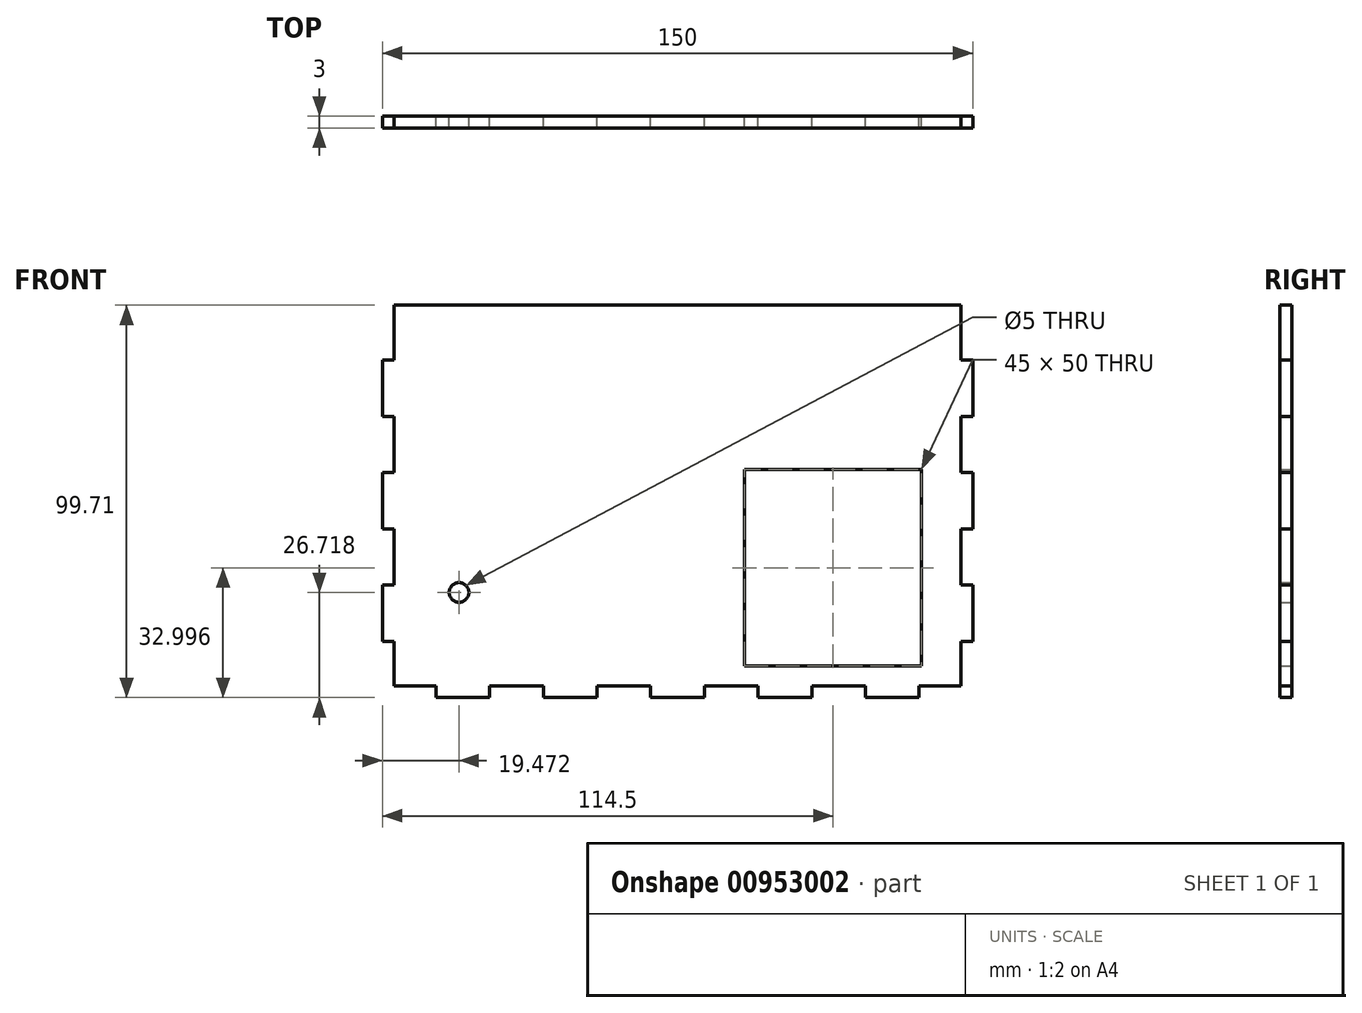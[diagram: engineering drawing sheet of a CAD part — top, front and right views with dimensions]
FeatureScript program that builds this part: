
annotation { "Feature Type Name" : "Feature", "Feature Type Description" : "" }
export const myFeature = defineFeature(function(context is Context, id is Id, definition is map)
    precondition{}
    {
        {
            var Q0;
            Q0=qCreatedBy(makeId("Front.planeOp"),FACE);
            var sketch = newSketch(context, id + "F0", { "sketchPlane" : qUnion([Q0])});
            skLineSegment(sketch, "E0.top", {"start": v(72, 50) * mm, "end": v(-72, 50) * mm});
            skLineSegment(sketch, "E1.bottom", {"start": v(61.36, -49.71) * mm, "end": v(47.73, -49.71) * mm});
            skLineSegment(sketch, "E2", {"start": v(-72, -46.71) * mm, "end": v(-61.36, -46.71) * mm});
            skLineSegment(sketch, "E3", {"start": v(-61.36, -46.71) * mm, "end": v(-61.36, -49.71) * mm});
            skLineSegment(sketch, "E4", {"start": v(-47.73, -46.71) * mm, "end": v(-47.73, -49.71) * mm});
            skLineSegment(sketch, "E5", {"start": v(-34.1, -46.71) * mm, "end": v(-34.1, -49.71) * mm});
            skLineSegment(sketch, "E6", {"start": v(-20.45, -46.71) * mm, "end": v(-20.45, -49.71) * mm});
            skLineSegment(sketch, "E7", {"start": v(-6.82, -46.71) * mm, "end": v(-6.82, -49.71) * mm});
            skLineSegment(sketch, "E8", {"start": v(6.82, -46.71) * mm, "end": v(6.82, -49.71) * mm});
            skLineSegment(sketch, "E9", {"start": v(34.1, -46.71) * mm, "end": v(34.1, -49.71) * mm});
            skLineSegment(sketch, "E10", {"start": v(47.73, -46.71) * mm, "end": v(47.73, -49.71) * mm});
            skLineSegment(sketch, "E11", {"start": v(20.45, -46.71) * mm, "end": v(20.45, -49.71) * mm});
            skLineSegment(sketch, "E12", {"start": v(61.36, -46.71) * mm, "end": v(61.36, -49.71) * mm});
            skLineSegment(sketch, "E13.trimOffspring", {"start": v(-47.73, -46.71) * mm, "end": v(-34.1, -46.71) * mm});
            skLineSegment(sketch, "E14.trimOffspring", {"start": v(-47.73, -49.71) * mm, "end": v(-61.36, -49.71) * mm});
            skLineSegment(sketch, "E15.trimOffspring", {"start": v(-20.45, -46.71) * mm, "end": v(-6.82, -46.71) * mm});
            skLineSegment(sketch, "E16.trimOffspring", {"start": v(-20.45, -49.71) * mm, "end": v(-34.1, -49.71) * mm});
            skLineSegment(sketch, "E17.trimOffspring", {"start": v(6.82, -46.71) * mm, "end": v(20.45, -46.71) * mm});
            skLineSegment(sketch, "E18.trimOffspring", {"start": v(6.82, -49.71) * mm, "end": v(-6.82, -49.71) * mm});
            skLineSegment(sketch, "E19.trimOffspring", {"start": v(34.1, -46.71) * mm, "end": v(47.73, -46.71) * mm});
            skLineSegment(sketch, "E20.trimOffspring", {"start": v(34.1, -49.71) * mm, "end": v(20.45, -49.71) * mm});
            skLineSegment(sketch, "E21.trimOffspring", {"start": v(61.36, -46.71) * mm, "end": v(72, -46.71) * mm});
            skPoint(sketch, "E22.orphan", {"position": v(-72.02, -53.11) * mm});
            skPoint(sketch, "E0.right.start.orphan", {"position": v(-75, -50) * mm});
            skLineSegment(sketch, "E23.right", {"start": v(-75, -35.43) * mm, "end": v(-75, -21.14) * mm});
            skPoint(sketch, "E24.orphan", {"position": v(-75, -49.71) * mm});
            skLineSegment(sketch, "E25", {"start": v(-72, 50.29) * mm, "end": v(-72, 36) * mm});
            skLineSegment(sketch, "E26", {"start": v(-75, 36) * mm, "end": v(-72, 36) * mm});
            skLineSegment(sketch, "E27", {"start": v(-75, 21.71) * mm, "end": v(-72, 21.71) * mm});
            skLineSegment(sketch, "E28", {"start": v(-75, 7.43) * mm, "end": v(-72, 7.43) * mm});
            skLineSegment(sketch, "E29", {"start": v(-75, -6.86) * mm, "end": v(-72, -6.86) * mm});
            skLineSegment(sketch, "E30", {"start": v(-75, -21.14) * mm, "end": v(-72, -21.14) * mm});
            skLineSegment(sketch, "E31", {"start": v(-75, -35.43) * mm, "end": v(-72, -35.43) * mm});
            skLineSegment(sketch, "E32.trimOffspring", {"start": v(-72, -35.43) * mm, "end": v(-72, -46.71) * mm});
            skLineSegment(sketch, "E33.trimOffspring", {"start": v(-75, -6.86) * mm, "end": v(-75, 7.43) * mm});
            skLineSegment(sketch, "E34.trimOffspring", {"start": v(-72, -6.86) * mm, "end": v(-72, -21.14) * mm});
            skLineSegment(sketch, "E35.trimOffspring", {"start": v(-75, 21.71) * mm, "end": v(-75, 36) * mm});
            skLineSegment(sketch, "E36.trimOffspring", {"start": v(-72, 21.71) * mm, "end": v(-72, 7.43) * mm});
            skPoint(sketch, "E37.orphan", {"position": v(-75, 50.29) * mm});
            skPoint(sketch, "E38.orphan", {"position": v(-75, 50) * mm});
            skPoint(sketch, "E39.orphan", {"position": v(75, -50) * mm});
            skLineSegment(sketch, "E40.MirrorCS", {"start": v(75, 36) * mm, "end": v(72, 36) * mm});
            skLineSegment(sketch, "E41.MirrorCS", {"start": v(75, -21.14) * mm, "end": v(72, -21.14) * mm});
            skLineSegment(sketch, "E42.MirrorCS", {"start": v(75, 21.71) * mm, "end": v(72, 21.71) * mm});
            skLineSegment(sketch, "E43.MirrorCS", {"start": v(75, -35.43) * mm, "end": v(72, -35.43) * mm});
            skLineSegment(sketch, "E44.MirrorCS", {"start": v(75, 7.43) * mm, "end": v(72, 7.43) * mm});
            skLineSegment(sketch, "E45.MirrorCS", {"start": v(75, -6.86) * mm, "end": v(72, -6.86) * mm});
            skPoint(sketch, "E46.MirrorP", {"position": v(75, 50) * mm});
            skLineSegment(sketch, "E47.MirrorCS", {"start": v(72, -6.86) * mm, "end": v(72, -21.14) * mm});
            skLineSegment(sketch, "E48.MirrorCS", {"start": v(72, 50.29) * mm, "end": v(72, 36) * mm});
            skPoint(sketch, "E49.MirrorP", {"position": v(75, 50.29) * mm});
            skLineSegment(sketch, "E50.MirrorCS", {"start": v(75, -6.86) * mm, "end": v(75, 7.43) * mm});
            skLineSegment(sketch, "E51.MirrorCS", {"start": v(72, 21.71) * mm, "end": v(72, 7.43) * mm});
            skLineSegment(sketch, "E52.MirrorCS", {"start": v(72, -35.43) * mm, "end": v(72, -46.71) * mm});
            skPoint(sketch, "E53.MirrorP", {"position": v(75, -49.71) * mm});
            skLineSegment(sketch, "E54.MirrorCS", {"start": v(75, -35.43) * mm, "end": v(75, -21.14) * mm});
            skPoint(sketch, "E55.MirrorP", {"position": v(72.02, -53.11) * mm});
            skLineSegment(sketch, "E56.MirrorCS", {"start": v(75, 21.71) * mm, "end": v(75, 36) * mm});
            skLineSegment(sketch, "E57.bottom", {"start": v(62, -41.71) * mm, "end": v(17, -41.71) * mm});
            skLineSegment(sketch, "E57.top", {"start": v(62, 8.29) * mm, "end": v(17, 8.29) * mm});
            skLineSegment(sketch, "E57.left", {"start": v(62, -41.71) * mm, "end": v(62, 8.29) * mm});
            skLineSegment(sketch, "E57.right", {"start": v(17, -41.71) * mm, "end": v(17, 8.29) * mm});
            skCircle(sketch, "E58", {"center": v(-55.53, -23) * mm, "radius": 2.5 * mm});
            skSolve(sketch);
        }
        {
            var Q0;
            {var subQ1=sQuery(id+"F0.wireOp",EDGE,"E0.top");Q0=makeQuery(id+"F0.imprint","IMPRINT",FACE,{"disambiguationData":[TD([[makeQuery(id+"F0.imprint","IMPRINT",EDGE,{"derivedFrom":subQ1}),1.0]])]});}
            extrude(context, id + "F1", {"entities" : qUnion([Q0]), "depth" : 3 * mm, "offsetDistance" : 25 * mm});
        }
    });
